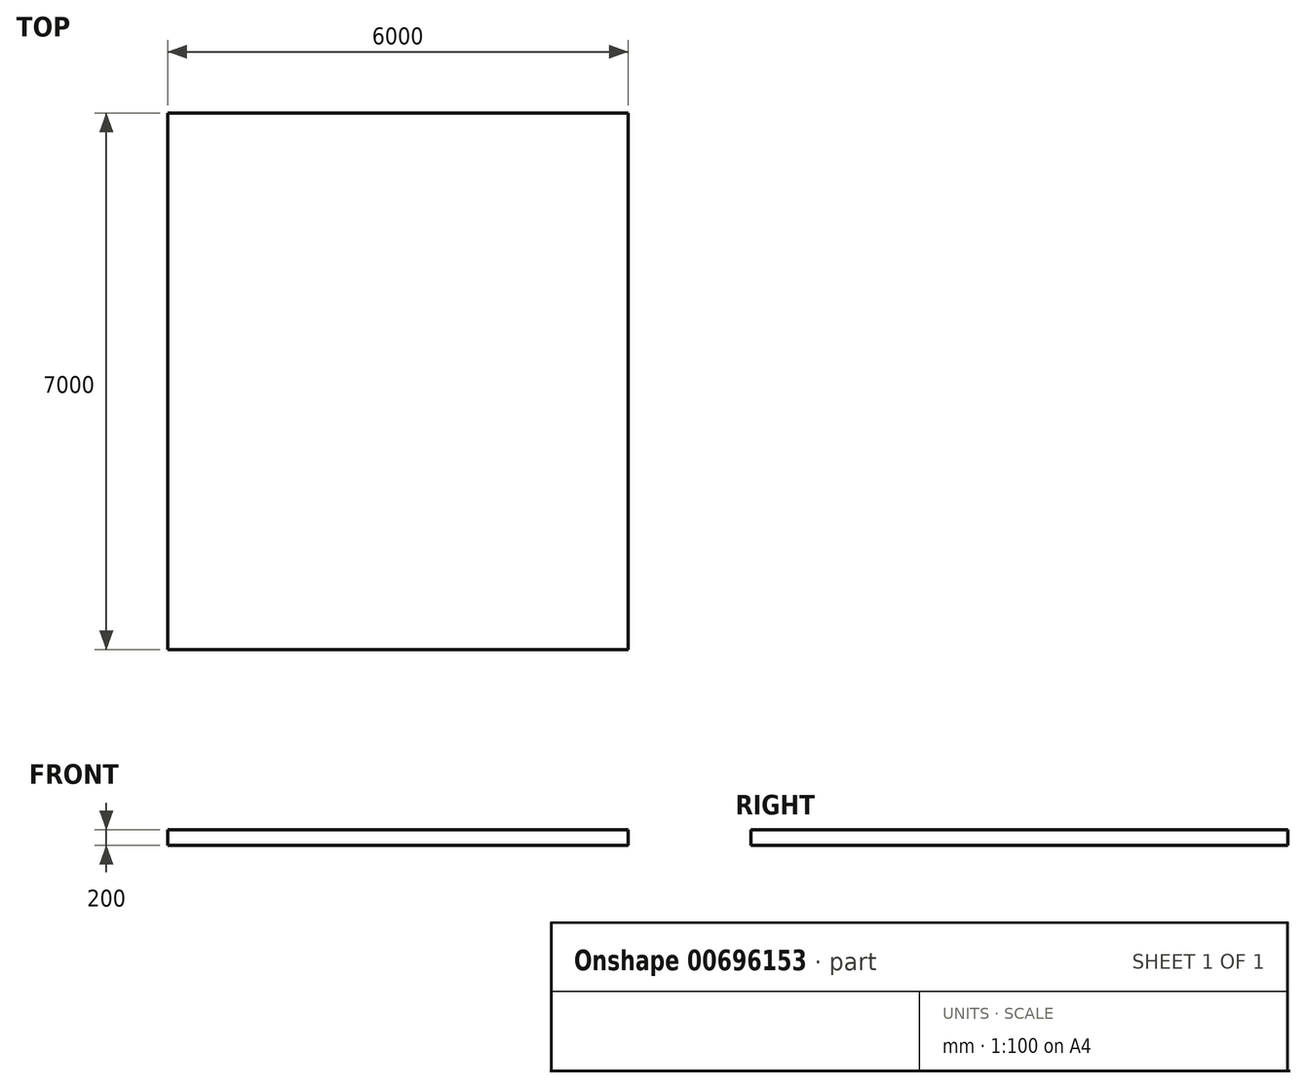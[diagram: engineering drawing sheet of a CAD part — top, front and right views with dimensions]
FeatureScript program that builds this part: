
annotation { "Feature Type Name" : "Feature", "Feature Type Description" : "" }
export const myFeature = defineFeature(function(context is Context, id is Id, definition is map)
    precondition{}
    {
        {
            var Q0;
            Q0=qCreatedBy(makeId("Top.planeOp"),FACE);
            var sketch = newSketch(context, id + "F0", { "sketchPlane" : qUnion([Q0])});
            skLineSegment(sketch, "E0.bottom", {"start": v(-2999.83, 4495.18) * mm, "end": v(3000.17, 4495.18) * mm});
            skLineSegment(sketch, "E0.top", {"start": v(-2999.83, -2504.82) * mm, "end": v(3000.17, -2504.82) * mm});
            skLineSegment(sketch, "E0.left", {"start": v(-2999.83, 4495.18) * mm, "end": v(-2999.83, -2504.82) * mm});
            skLineSegment(sketch, "E0.right", {"start": v(3000.17, 4495.18) * mm, "end": v(3000.17, -2504.82) * mm});
            skSolve(sketch);
        }
        {
            var Q0;
            Q0 = qSketchRegion(id + "F0", true);
            extrude(context, id + "F1", {"entities" : qUnion([Q0]), "oppositeDirection" : true, "depth" : 200 * mm, "offsetDistance" : 25 * mm});
        }
    });
